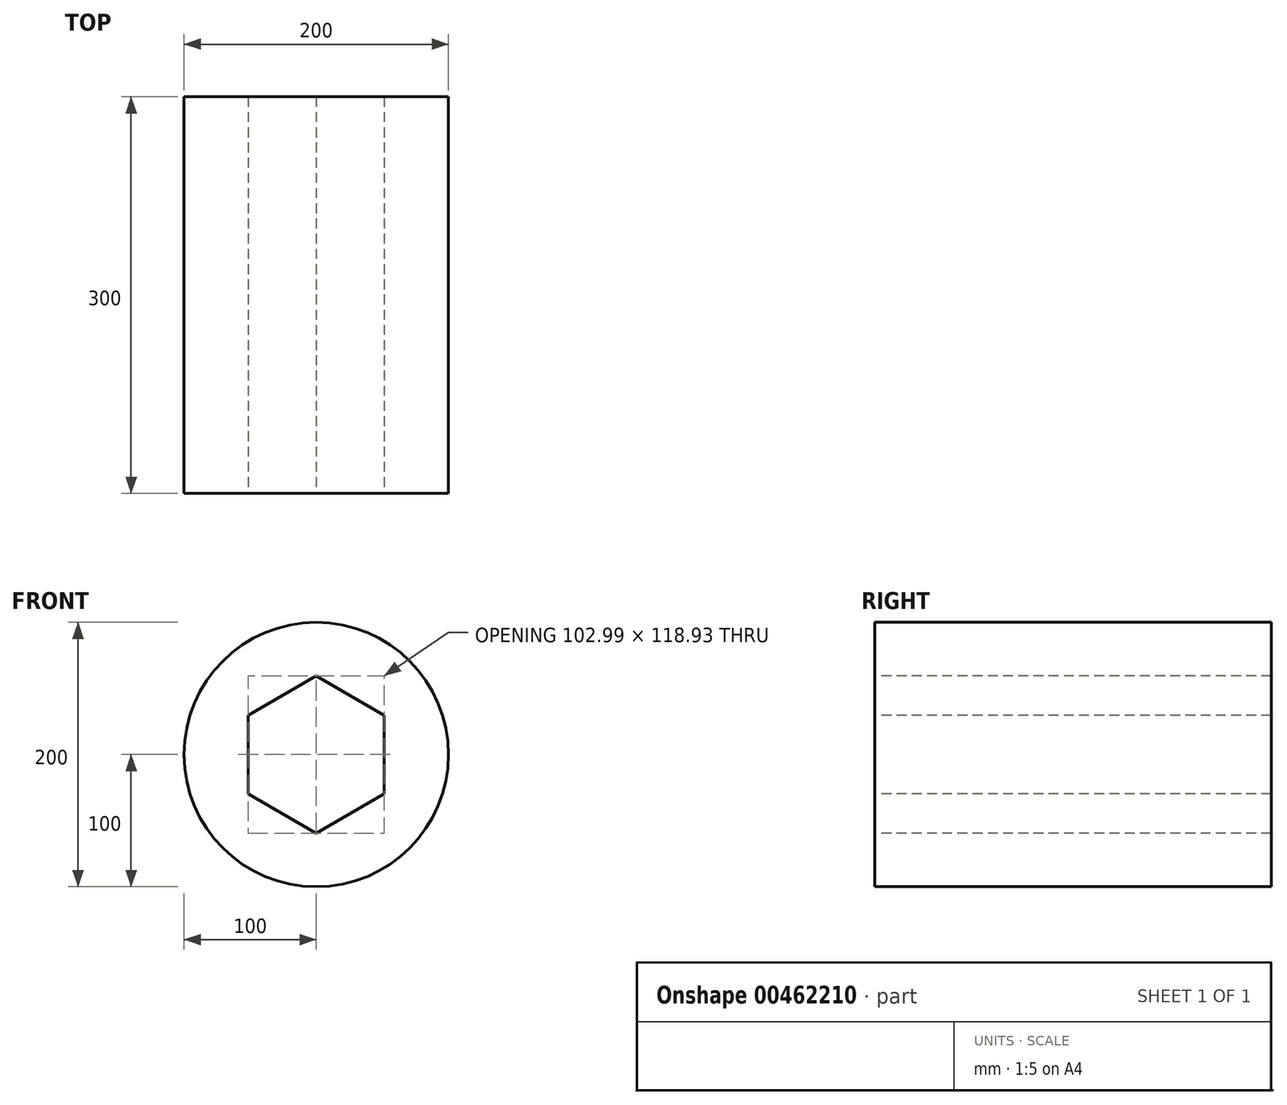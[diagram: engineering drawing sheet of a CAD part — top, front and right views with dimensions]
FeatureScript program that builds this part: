
annotation { "Feature Type Name" : "Feature", "Feature Type Description" : "" }
export const myFeature = defineFeature(function(context is Context, id is Id, definition is map)
    precondition{}
    {
        {
            var Q0;
            Q0=qCreatedBy(makeId("Front.planeOp"),FACE);
            var sketch = newSketch(context, id + "F0", { "sketchPlane" : qUnion([Q0])});
            skCircle(sketch, "E0", {"center": v(0, 0) * mm, "radius": 100 * mm});
            skSolve(sketch);
        }
        {
            var Q0;
            Q0=makeQuery(id+"F0.imprint","IMPRINT",FACE,{"disambiguationData":[TD([[makeQuery(id+"F0.imprint","IMPRINT",EDGE,{"derivedFrom":sQuery(id+"F0.wireOp",EDGE,"E0")}),1.0]])]});
            extrude(context, id + "F1", {"entities" : qUnion([Q0]), "depth" : 300 * mm});
        }
        {
            var Q0;
            Q0=makeQuery(id+"F1.opExtrude","CAP_FACE",FACE,{"disambiguationData":[OSD([sQuery(id+"F0.wireOp",EDGE,"E0")])],"isStart":false});
            var sketch = newSketch(context, id + "F2", { "sketchPlane" : qUnion([Q0])});
            skCircle(sketch, "E1.cCircle", {"center": v(0, 0) * mm, "radius": 51.5 * mm, "construction": true});
            skLineSegment(sketch, "E1.0", {"start": v(51.5, 29.73) * mm, "end": v(51.5, -29.73) * mm});
            skLineSegment(sketch, "E1.1", {"start": v(51.5, -29.73) * mm, "end": v(0, -59.46) * mm});
            skLineSegment(sketch, "E1.2", {"start": v(0, -59.46) * mm, "end": v(-51.5, -29.73) * mm});
            skLineSegment(sketch, "E1.3", {"start": v(-51.5, -29.73) * mm, "end": v(-51.5, 29.73) * mm});
            skLineSegment(sketch, "E1.4", {"start": v(-51.5, 29.73) * mm, "end": v(0, 59.46) * mm});
            skLineSegment(sketch, "E1.5", {"start": v(0, 59.46) * mm, "end": v(51.5, 29.73) * mm});
            skPoint(sketch, "E1.0.midPoint", {"position": v(51.5, 0) * mm});
            skSolve(sketch);
        }
        {
            var Q0;
            Q0 = qSketchRegion(id + "F2", true);
            extrude(context, id + "F3", {"entities" : qUnion([Q0]), "operationType" : NewBodyOperationType.REMOVE, "oppositeDirection" : true, "depth" : 300 * mm});
        }
    });
